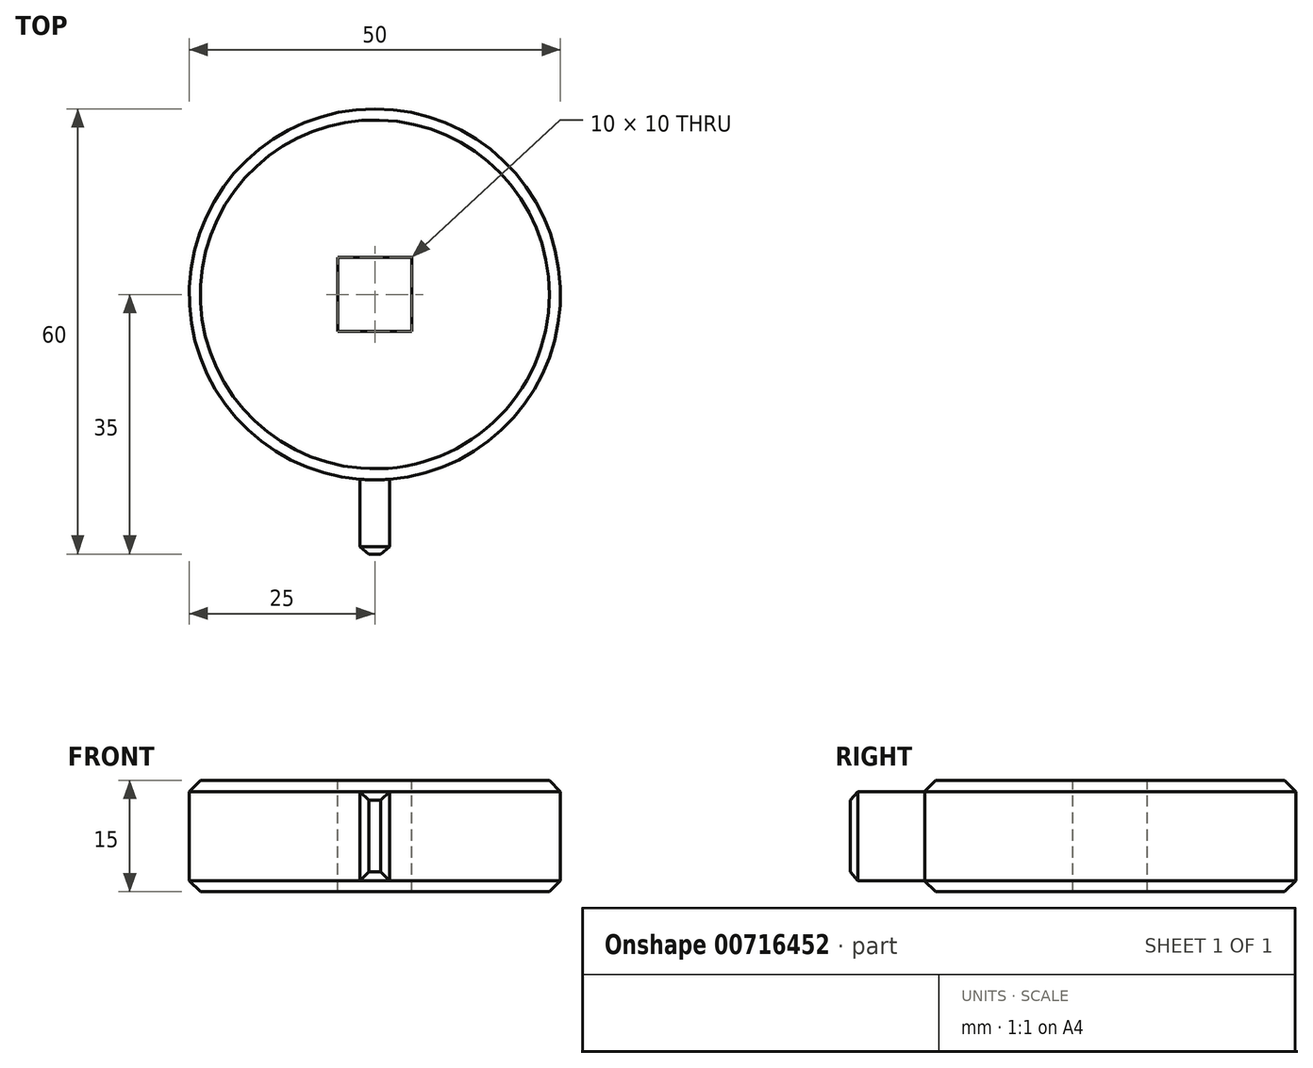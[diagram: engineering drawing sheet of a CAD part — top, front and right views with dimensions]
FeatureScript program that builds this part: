
annotation { "Feature Type Name" : "Feature", "Feature Type Description" : "" }
export const myFeature = defineFeature(function(context is Context, id is Id, definition is map)
    precondition{}
    {
        {
            var Q0;
            Q0=qCreatedBy(makeId("Top.planeOp"),FACE);
            var sketch = newSketch(context, id + "F0", { "sketchPlane" : qUnion([Q0])});
            skCircle(sketch, "E0", {"center": v(0, 0) * mm, "radius": 25 * mm});
            skSolve(sketch);
        }
        {
            var Q0;
            Q0=makeQuery(id+"F0.imprint","IMPRINT",FACE,{"disambiguationData":[TD([[makeQuery(id+"F0.imprint","IMPRINT",EDGE,{"derivedFrom":sQuery(id+"F0.wireOp",EDGE,"E0")}),1.0]])]});
            extrude(context, id + "F1", {"entities" : qUnion([Q0]), "depth" : 15 * mm, "offsetDistance" : 25 * mm});
        }
        {
            var Q0;
            Q0=makeQuery(id+"F1.opExtrude","CAP_FACE",FACE,{"disambiguationData":[OSD([sQuery(id+"F0.wireOp",EDGE,"E0")])],"isStart":false});
            var sketch = newSketch(context, id + "F2", { "sketchPlane" : qUnion([Q0])});
            skLineSegment(sketch, "E1.bottom", {"start": v(-5, -5) * mm, "end": v(5, -5) * mm});
            skLineSegment(sketch, "E1.top", {"start": v(-5, 5) * mm, "end": v(5, 5) * mm});
            skLineSegment(sketch, "E1.left", {"start": v(-5, -5) * mm, "end": v(-5, 5) * mm});
            skLineSegment(sketch, "E1.right", {"start": v(5, -5) * mm, "end": v(5, 5) * mm});
            skPoint(sketch, "E1.middle", {"position": v(0, 0) * mm});
            skSolve(sketch);
        }
        {
            var Q0;
            Q0=makeQuery(id+"F2.imprint","IMPRINT",FACE,{"disambiguationData":[TD([[makeQuery(id+"F2.imprint","IMPRINT",EDGE,{"derivedFrom":sQuery(id+"F2.wireOp",EDGE,"E1.bottom")}),1.0]])]});
            extrude(context, id + "F3", {"entities" : qUnion([Q0]), "operationType" : NewBodyOperationType.REMOVE, "oppositeDirection" : true, "depth" : 15 * mm, "offsetDistance" : 25 * mm});
        }
        {
            var Q0;
            Q0=qCreatedBy(makeId("Front.planeOp"),FACE);
            cPlane(context, id + "F4", {"entities" : qUnion([Q0]), "cplaneType" : CPlaneType.OFFSET, "offset" : 25 * mm, "width" : 150 * mm, "height" : 150 * mm});
        }
        {
            var Q0;
            Q0=qCreatedBy(id+"F4.planeOp",FACE);
            var sketch = newSketch(context, id + "F5", { "sketchPlane" : qUnion([Q0])});
            skLineSegment(sketch, "E2.bottom", {"start": v(2, 1.5) * mm, "end": v(-2, 1.5) * mm});
            skLineSegment(sketch, "E2.top", {"start": v(2, 13.5) * mm, "end": v(-2, 13.5) * mm});
            skLineSegment(sketch, "E2.left", {"start": v(2, 1.5) * mm, "end": v(2, 13.5) * mm});
            skLineSegment(sketch, "E2.right", {"start": v(-2, 1.5) * mm, "end": v(-2, 13.5) * mm});
            skPoint(sketch, "E2.middle", {"position": v(0, 7.5) * mm});
            skSolve(sketch);
        }
        {
            var Q0;
            Q0=makeQuery(id+"F5.imprint","IMPRINT",FACE,{"disambiguationData":[TD([[makeQuery(id+"F5.imprint","IMPRINT",EDGE,{"derivedFrom":sQuery(id+"F5.wireOp",EDGE,"E2.bottom")}),-1.0]])]});
            extrude(context, id + "F6", {"entities" : qUnion([Q0]), "operationType" : NewBodyOperationType.ADD, "depth" : 10 * mm, "offsetDistance" : 25 * mm, "hasSecondDirection" : true, "secondDirectionOppositeDirection" : true, "secondDirectionDepth" : 5 * mm});
        }
        {
            var Q0;
            Q0=makeQuery(id+"F1.opExtrude","CAP_EDGE",EDGE,{"disambiguationData":[OSD([sQuery(id+"F0.wireOp",EDGE,"E0")])],"isStart":false});
            var Q1;
            Q1=makeQuery(id+"F3.boolean.opBoolean","COPY",EDGE,{"derivedFrom":makeQuery(id+"F3.opExtrude","CAP_EDGE",EDGE,{"disambiguationData":[OSD([sQuery(id+"F2.wireOp",EDGE,"E1.top")])],"isStart":true})});
            var Q2;
            Q2=makeQuery(id+"F3.boolean.opBoolean","COPY",EDGE,{"derivedFrom":makeQuery(id+"F3.opExtrude","CAP_EDGE",EDGE,{"disambiguationData":[OSD([sQuery(id+"F2.wireOp",EDGE,"E1.bottom")])],"isStart":true})});
            var Q3;
            Q3=makeQuery(id+"F3.boolean.opBoolean","COPY",EDGE,{"derivedFrom":makeQuery(id+"F3.opExtrude","CAP_EDGE",EDGE,{"disambiguationData":[OSD([sQuery(id+"F2.wireOp",EDGE,"E1.left")])],"isStart":true})});
            var Q4;
            Q4=makeQuery(id+"F3.boolean.opBoolean","COPY",EDGE,{"derivedFrom":makeQuery(id+"F3.opExtrude","CAP_EDGE",EDGE,{"disambiguationData":[OSD([sQuery(id+"F2.wireOp",EDGE,"E1.right")])],"isStart":true})});
            var Q5;
            Q5=makeQuery(id+"F1.opExtrude","CAP_EDGE",EDGE,{"disambiguationData":[OSD([sQuery(id+"F0.wireOp",EDGE,"E0")])],"isStart":true});
            var Q6;
            Q6=makeQuery(id+"F3.boolean.opBoolean","COPY",EDGE,{"derivedFrom":makeQuery(id+"F3.opExtrude","CAP_EDGE",EDGE,{"disambiguationData":[OSD([sQuery(id+"F2.wireOp",EDGE,"E1.bottom")])],"isStart":false})});
            var Q7;
            Q7=makeQuery(id+"F3.boolean.opBoolean","COPY",EDGE,{"derivedFrom":makeQuery(id+"F3.opExtrude","CAP_EDGE",EDGE,{"disambiguationData":[OSD([sQuery(id+"F2.wireOp",EDGE,"E1.left")])],"isStart":false})});
            var Q8;
            Q8=makeQuery(id+"F3.boolean.opBoolean","COPY",EDGE,{"derivedFrom":makeQuery(id+"F3.opExtrude","CAP_EDGE",EDGE,{"disambiguationData":[OSD([sQuery(id+"F2.wireOp",EDGE,"E1.right")])],"isStart":false})});
            var Q9;
            Q9=makeQuery(id+"F3.boolean.opBoolean","COPY",EDGE,{"derivedFrom":makeQuery(id+"F3.opExtrude","CAP_EDGE",EDGE,{"disambiguationData":[OSD([sQuery(id+"F2.wireOp",EDGE,"E1.top")])],"isStart":false})});
            chamfer(context, id + "F7", {"entities" : qUnion([Q0, Q1, Q2, Q3, Q4, Q5, Q6, Q7, Q8, Q9]), "width" : 1.5 * mm, "tangentPropagation" : true});
        }
        {
            var Q0;
            Q0=makeQuery(id+"F311k2O5QvPxUnV_2.4.F6.opExtrude","CAP_FACE",FACE,{"disambiguationData":[OSD([sQuery(id+"F5.wireOp",EDGE,"E2.bottom"),sQuery(id+"F5.wireOp",EDGE,"E2.top"),sQuery(id+"F5.wireOp",EDGE,"E2.left"),sQuery(id+"F5.wireOp",EDGE,"E2.right")])],"isStart":false});
            var Q1;
            Q1=makeQuery(id+"F311k2O5QvPxUnV_2.3.F6.opExtrude","CAP_FACE",FACE,{"disambiguationData":[OSD([sQuery(id+"F5.wireOp",EDGE,"E2.bottom"),sQuery(id+"F5.wireOp",EDGE,"E2.top"),sQuery(id+"F5.wireOp",EDGE,"E2.left"),sQuery(id+"F5.wireOp",EDGE,"E2.right")])],"isStart":false});
            var Q2;
            Q2=makeQuery(id+"F311k2O5QvPxUnV_2.2.F6.opExtrude","CAP_FACE",FACE,{"disambiguationData":[OSD([sQuery(id+"F5.wireOp",EDGE,"E2.bottom"),sQuery(id+"F5.wireOp",EDGE,"E2.top"),sQuery(id+"F5.wireOp",EDGE,"E2.left"),sQuery(id+"F5.wireOp",EDGE,"E2.right")])],"isStart":false});
            var Q3;
            Q3=makeQuery(id+"F311k2O5QvPxUnV_2.1.F6.opExtrude","CAP_FACE",FACE,{"disambiguationData":[OSD([sQuery(id+"F5.wireOp",EDGE,"E2.bottom"),sQuery(id+"F5.wireOp",EDGE,"E2.top"),sQuery(id+"F5.wireOp",EDGE,"E2.left"),sQuery(id+"F5.wireOp",EDGE,"E2.right")])],"isStart":false});
            var Q4;
            Q4=makeQuery(id+"F6.opExtrude","CAP_FACE",FACE,{"disambiguationData":[OSD([sQuery(id+"F5.wireOp",EDGE,"E2.bottom"),sQuery(id+"F5.wireOp",EDGE,"E2.top"),sQuery(id+"F5.wireOp",EDGE,"E2.left"),sQuery(id+"F5.wireOp",EDGE,"E2.right")])],"isStart":false});
            var Q5;
            Q5=makeQuery(id+"F311k2O5QvPxUnV_2.7.F6.opExtrude","CAP_FACE",FACE,{"disambiguationData":[OSD([sQuery(id+"F5.wireOp",EDGE,"E2.bottom"),sQuery(id+"F5.wireOp",EDGE,"E2.top"),sQuery(id+"F5.wireOp",EDGE,"E2.left"),sQuery(id+"F5.wireOp",EDGE,"E2.right")])],"isStart":false});
            var Q6;
            Q6=makeQuery(id+"F311k2O5QvPxUnV_2.6.F6.opExtrude","CAP_FACE",FACE,{"disambiguationData":[OSD([sQuery(id+"F5.wireOp",EDGE,"E2.bottom"),sQuery(id+"F5.wireOp",EDGE,"E2.top"),sQuery(id+"F5.wireOp",EDGE,"E2.left"),sQuery(id+"F5.wireOp",EDGE,"E2.right")])],"isStart":false});
            var Q7;
            Q7=makeQuery(id+"F311k2O5QvPxUnV_2.5.F6.opExtrude","CAP_FACE",FACE,{"disambiguationData":[OSD([sQuery(id+"F5.wireOp",EDGE,"E2.bottom"),sQuery(id+"F5.wireOp",EDGE,"E2.top"),sQuery(id+"F5.wireOp",EDGE,"E2.left"),sQuery(id+"F5.wireOp",EDGE,"E2.right")])],"isStart":false});
            chamfer(context, id + "F8", {"entities" : qUnion([Q0, Q1, Q2, Q3, Q4, Q5, Q6, Q7]), "chamferType" : ChamferType.OFFSET_ANGLE, "width" : 1 * mm, "oppositeDirection" : false, "angle" : 50 * degree, "tangentPropagation" : true});
        }
    });
